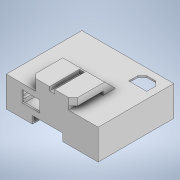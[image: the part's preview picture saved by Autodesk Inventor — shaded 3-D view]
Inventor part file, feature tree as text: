
AUTODESK INVENTOR PART (.ipt)
format: ipt  version: 2022 (Build 260153000, 153)  size: 356,864 bytes
history: native  units: in
note: dims shown in document units (in); Inventor stores cm internally (conversion verified against a paired STEP export)
features: extrude x15, sketch x14, chamfer x2
ambient origin geometry x8: Origin, YZ Plane, XZ Plane, XY Plane, X Axis, Y Axis, Z Axis, Center Point
bodies: Solid1 (feature_tree)
feature tree (31):
  sketch  "Sketch1"  dims[d0=2.2047in d1=1.9685in]
  extrude  "Extrusion1"  Depth=1.9685in
  extrude  "Extrusion2"  Depth=0.0079in
  extrude  "Extrusion3"  TaperAngle=0.0deg  [1 undecoded]
  extrude  "Extrusion5"  Depth=0.0984in
  extrude  "Extrusion6"  Depth=0.0984in
  extrude  "Extrusion7"  Depth=0.0394in TaperAngle=0.0deg
  extrude  "Extrusion8"  Depth=0.0984in
  extrude  "Extrusion9"  Depth=0.0394in
  extrude  "Extrusion10"  TaperAngle=0.0deg  [1 undecoded]
  extrude  "Extrusion11"  Depth=0.0394in
  extrude  "Extrusion12"  TaperAngle=0.0deg  [1 undecoded]
  extrude  "Extrusion13"  Depth=0.8268in
  extrude  "Extrusion14"  Depth=0.1969in
  extrude  "Extrusion15"  Depth=0.2953in
  extrude  "Extrusion16"  Depth=0.0787in
  chamfer  "Chamfer1"  Distance=0.7087in
  chamfer  "Chamfer2"  Distance=0.3543in
  sketch  "Sketch2"  dims[d2=0.0079in d3=0.0079in]
  sketch  "Sketch3"  dims[d4=0.0in d5=0.0in]
  sketch  "Sketch4"  dims[d6=0.0984in d7=0.0984in]
  sketch  "Sketch5"  dims[d8=0.0984in d9=0.0984in]
  sketch  "Sketch6"  dims[d10=0.5984in d11=0.0in d12=0.0394in d13=0.0in]
  sketch  "Sketch7"  dims[d14=0.0in d16=0.0984in]
  sketch  "Sketch8"  dims[d17=0.0394in d18=0.0394in]
  sketch  "Sketch9"  dims[d19=0.0in d20=0.0in]
  sketch  "Sketch10"  dims[d21=0.0669in d22=0.0394in]
  sketch  "Sketch11"  dims[d23=0.0984in d24=0.0in]
  sketch  "Sketch12"  dims[d25=0.5906in d26=0.8268in]
  sketch  "Sketch13"  dims[d27=0.0in d30=0.1969in]
  sketch  "Sketch14"  dims[d31=2.9813in d32=0.0in d33=0.2953in d34=0.4331in d35=0.7087in d36=0.3543in d37=2.9813in d38=0.0in d39=0.1181in d40=0.0in d41=1.4173in d42=1.6535in d43=0.0787in d44=0.5512in d45=0.1181in d46=0.1181in d47=45.0deg d48=135.0deg d49=0.1181in d50=0.0394in d51=0.0in d52=0.0394in d53=0.0394in d54=0.0394in d55=0.0394in d56=0.3937in d57=0.0in d58=0.1181in d59=0.3937in d60=0.0in d61=0.0394in d62=0.0in d63=0.0394in d64=0.0394in d65=0.0in d66=0.0591in d67=0.9813in d68=0.0in d69=0.0787in d70=0.0787in d71=0.0787in d73=0.0394in d74=0.9813in d75=0.0in d76=0.0in d77=0.0984in d78=0.8661in d79=2.4173in d80=0.7756in d81=0.1883in d82=0.0in d83=1.1014in d84=0.658in d85=0.0965in d86=0.1339in d87=0.0in d88=1.1417in d89=0.7874in d90=0.0in d91=0.0in d92=0.0in d93=0.0394in d94=0.0in d95=0.1176in d96=0.0787in d97=45.0deg d98=0.2867in d99=0.0787in d100=45.0deg]
note: 3 required parameter values undecoded (feature->parameter linkage not recoverable at this tier; creation-order binding heuristic only, values carry confidence <= 0.55)
